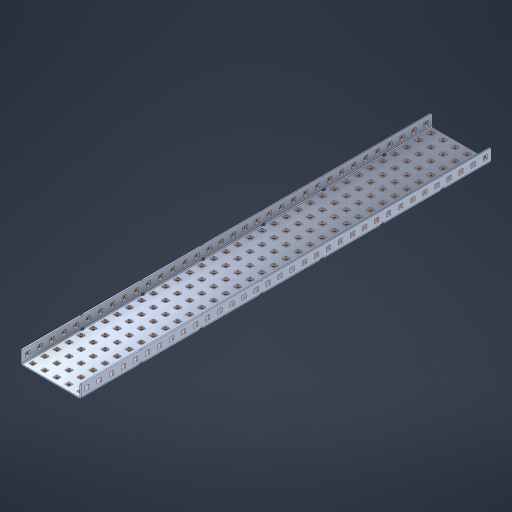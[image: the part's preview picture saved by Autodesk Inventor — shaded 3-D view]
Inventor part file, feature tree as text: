
AUTODESK INVENTOR PART (.ipt)
format: ipt  version: 2023 (Build 270158000, 158)  size: 2,476,032 bytes
history: native  units: in
note: dims shown in document units (in); Inventor stores cm internally (conversion verified against a paired STEP export)
features: other x243, extrude x237, sheet_metal_op x10, sketch x8, mirror x1, pattern_linear x1, chamfer x1
ambient origin geometry x8: Origin, YZ Plane, XZ Plane, XY Plane, X Axis, Y Axis, Z Axis, Center Point
bodies: Solid1 (feature_tree), Body (feature_tree)
feature tree (501):
  other  "Flange Pattern Plane"
  sheet_metal_op  "Flange Pattern"
  sheet_metal_op  "Body Pattern"
  other  "Arc Length"
  mirror  "Notch Mirror"
  pattern_linear  "Notch Pattern"  Spacing1=0.1875in  [1 undecoded]
  chamfer  "End Chamfer"
  extrude  "Half Cut"  Depth=0.0469in
  sketch  "Sketch1"  dims[d0=2.5in]
  other  "Plate1"
  sketch  "Sketch2"  dims[d1=17.0in]
  other  "Plate2"
  sheet_metal_op  "Bend1"
  sheet_metal_op  "Corner1"
  sketch  "Sketch3"  dims[d2=0.0469in]
  other  "Flange Pattern Sketch"
  sketch  "Sketch7"  dims[d3=0.0469in]
  other  "Srf1"
  other  "Srf2"
  sketch  "Sketch8"  dims[d4=0.0234in]
  sketch  "Sketch9"  dims[d5=0.0938in]
  other  "Srf91"
  sheet_metal_op  "Body Pattern Sketch"
  other  "Srf92"
  sketch  "Sketch13"  dims[d6=0.0469in]
  sketch  "Sketch14"  dims[d7=0.5in d8=90.0deg d9=0.0312in d10=0.1875in d11=0.0469in d12=0.0469in d16=0.182in d17=0.02in d18=0.0469in d19=0.0in d20=0.25in d21=0.25in d46=0.172in d47=1.0in d48=0.0in d49=0.182in d50=0.02in d51=0.25in d52=0.25in d53=0.0469in d54=0.0in d55=0.172in d56=1.0in d57=0.0in d60=13.3858in d62=0.5in d63=1.9685in d65=0.5in d85=0.1227in d86=0.1659in d88=0.04in d89=0.0469in d90=0.0in d91=0.04in d92=0.0491in d95=2.5in d96=0.04in d97=0.25in d98=45.0deg d101=0.0in d102=2.497in d131=2.5in d132=13.3858in d134=0.5in d139=0.5in]
  other  "Srf856"
  other  "Srf1310"
  other  "Srf1311"
  other  "Srf1312"
  other  "Srf1376"
  other  "Srf1377"
  other  "Srf1728"
  other  "Srf1755"
  other  "Srf1878"
  other  "Srf1879"
  other  "Srf1880"
  other  "Srf1881"
  other  "Srf1882"
  other  "Srf1883"
  other  "Srf1884"
  other  "Srf1885"
  other  "Srf1886"
  other  "Srf1887"
  other  "Srf1888"
  other  "Srf1889"
  other  "Srf1890"
  other  "Srf1891"
  other  "Srf1892"
  other  "Srf1893"
  other  "Srf1894"
  other  "Srf1895"
  other  "Srf1896"
  other  "Srf1897"
  other  "Srf1898"
  other  "Srf1899"
  other  "Srf1900"
  other  "Srf1901"
  other  "Srf1902"
  other  "Srf1903"
  other  "Srf1904"
  other  "Srf1905"
  other  "Srf1906"
  other  "Srf1942"
  other  "Srf1943"
  other  "Srf1944"
  other  "Srf1945"
  other  "Srf1946"
  other  "Srf1947"
  other  "Srf1948"
  other  "Srf1949"
  other  "Srf1950"
  other  "Srf1951"
  other  "Srf1952"
  other  "Srf1953"
  other  "Srf1954"
  other  "Srf1955"
  other  "Srf1956"
  other  "Srf1957"
  other  "Srf1958"
  other  "Srf1959"
  other  "Srf1960"
  other  "Srf1961"
  other  "Srf1962"
  other  "Srf1963"
  other  "Srf1964"
  other  "Srf1965"
  other  "Srf1966"
  other  "Srf1967"
  other  "Srf1968"
  other  "Srf1969"
  other  "Srf1970"
  other  "Srf2111"
  other  "Srf2112"
  other  "Srf2113"
  other  "Srf2114"
  other  "Srf2115"
  other  "Srf2116"
  other  "Srf2117"
  other  "Srf2118"
  other  "Srf2119"
  other  "Srf2120"
  other  "Srf2121"
  other  "Srf2122"
  other  "Srf2123"
  other  "Srf2124"
  other  "Srf2125"
  other  "Srf2126"
  other  "Srf2127"
  other  "Srf2128"
  other  "Srf2129"
  other  "Srf2130"
  other  "Srf2131"
  other  "Srf2132"
  other  "Srf2133"
  other  "Srf2134"
  other  "Srf2135"
  other  "Srf2136"
  other  "Srf2137"
  other  "Srf2138"
  other  "Srf2139"
  other  "Srf2140"
  other  "Srf2141"
  other  "Srf2142"
  other  "Srf2143"
  other  "Srf2146"
  other  "Srf2147"
  other  "Srf2148"
  other  "Srf2149"
  other  "Srf2150"
  other  "Srf2151"
  other  "Srf2152"
  other  "Srf2153"
  other  "Srf2154"
  other  "Srf2155"
  other  "Srf2156"
  other  "Srf2157"
  other  "Srf2158"
  other  "Srf2159"
  other  "Srf2160"
  other  "Srf2161"
  other  "Srf2162"
  other  "Srf2163"
  other  "Srf2164"
  other  "Srf2165"
  other  "Srf2166"
  other  "Srf2167"
  other  "Srf2168"
  other  "Srf2169"
  other  "Srf2170"
  other  "Srf2171"
  other  "Srf2172"
  other  "Srf2173"
  other  "Srf2174"
  other  "Srf2175"
  other  "Srf2176"
  other  "Srf2177"
  other  "Srf2178"
  other  "Srf2179"
  other  "Srf2180"
  other  "Srf2181"
  other  "Srf2182"
  other  "Srf2183"
  other  "Srf2184"
  other  "Srf2185"
  other  "Srf2186"
  other  "Srf2187"
  other  "Srf2188"
  other  "Srf2189"
  other  "Srf2190"
  other  "Srf2191"
  other  "Srf2192"
  other  "Srf2193"
  other  "Srf2194"
  other  "Srf2195"
  other  "Srf2196"
  other  "Srf2197"
  other  "Srf2198"
  other  "Srf2199"
  other  "Srf2200"
  other  "Srf2201"
  other  "Srf2202"
  other  "Srf2203"
  other  "Srf2204"
  other  "Srf2205"
  other  "Srf2206"
  other  "Srf2207"
  other  "Srf2208"
  other  "Srf2209"
  other  "Srf2210"
  other  "Srf2211"
  other  "Srf2212"
  other  "Srf2213"
  other  "Srf2214"
  other  "Srf2215"
  other  "Srf2216"
  other  "Srf2217"
  other  "Srf2218"
  other  "Srf2219"
  other  "Srf2220"
  other  "Srf2221"
  other  "Srf2222"
  other  "Srf2223"
  other  "Srf2224"
  other  "Srf2225"
  other  "Srf2226"
  other  "Srf2227"
  other  "Srf2228"
  other  "Srf2229"
  other  "Srf2230"
  other  "Srf2231"
  other  "Srf2232"
  other  "Srf2233"
  other  "Srf2234"
  other  "Srf2235"
  other  "Srf2236"
  other  "Srf2237"
  other  "Srf2238"
  other  "Srf2239"
  other  "Srf2240"
  other  "Srf2241"
  other  "Srf2242"
  other  "Srf2243"
  other  "Srf2244"
  other  "Srf2245"
  other  "Srf2246"
  other  "Srf2247"
  other  "Srf2248"
  other  "Srf2249"
  other  "Srf2250"
  other  "Srf2251"
  other  "Srf2252"
  other  "Srf2253"
  other  "Srf2254"
  other  "Srf2255"
  other  "Srf2256"
  other  "Srf2257"
  other  "Srf2258"
  other  "Srf2259"
  other  "Srf2260"
  other  "Srf2261"
  other  "Srf2262"
  other  "Srf2263"
  other  "Srf2264"
  other  "Srf2265"
  other  "Srf2266"
  other  "Srf2267"
  other  "Srf2268"
  other  "Srf2269"
  other  "Srf2270"
  other  "Srf2271"
  other  "Srf2272"
  other  "Srf2273"
  other  "Srf2274"
  other  "Srf2275"
  other  "Srf2276"
  other  "Srf2277"
  other  "Srf2278"
  other  "Srf2279"
  other  "Srf2280"
  sheet_metal_op  "Flange Stamp"
  sheet_metal_op  "Flange Circle"
  sheet_metal_op  "Body Stamp"
  sheet_metal_op  "Body Circle"
  sheet_metal_op  "Notch"
  extrude  "ExtrusionSrf2"  Depth=0.0469in
  extrude  "ExtrusionSrf92"  Depth=2.5in
  extrude  "ExtrusionSrf856"  Depth=0.02in
  extrude  "ExtrusionSrf1310"  Depth=0.0469in
  extrude  "ExtrusionSrf1311"  TaperAngle=0.0deg  [1 undecoded]
  extrude  "ExtrusionSrf1312"  Depth=0.25in
  extrude  "ExtrusionSrf1376"  Depth=0.25in
  extrude  "ExtrusionSrf1377"  Depth=2.5in
  extrude  "ExtrusionSrf1728"  Depth=2.5in TaperAngle=0.0deg
  extrude  "ExtrusionSrf1755"  Depth=2.5in
  extrude  "ExtrusionSrf1878"  Depth=0.02in
  extrude  "ExtrusionSrf1879"  Depth=0.25in
  extrude  "ExtrusionSrf1880"  Depth=0.25in
  extrude  "ExtrusionSrf1881"  Depth=0.0469in
  extrude  "ExtrusionSrf1882"  TaperAngle=0.0deg  [1 undecoded]
  extrude  "ExtrusionSrf1883"  Depth=2.5in
  extrude  "ExtrusionSrf1884"  Depth=2.5in TaperAngle=0.0deg
  extrude  "ExtrusionSrf1885"  Depth=2.5in
  extrude  "ExtrusionSrf1886"  Depth=2.5in
  extrude  "ExtrusionSrf1887"  Depth=2.5in
  extrude  "ExtrusionSrf1888"  Depth=2.5in
  extrude  "ExtrusionSrf1889"  Depth=2.5in
  extrude  "ExtrusionSrf1890"  Depth=0.0469in
  extrude  "ExtrusionSrf1891"  TaperAngle=0.0deg  [1 undecoded]
  extrude  "ExtrusionSrf1892"  Depth=2.5in
  extrude  "ExtrusionSrf1893"  Depth=2.5in
  extrude  "ExtrusionSrf1894"  Depth=2.5in
  extrude  "ExtrusionSrf1895"  Depth=0.25in TaperAngle=45.0deg
  extrude  "ExtrusionSrf1896"  TaperAngle=0.0deg  [1 undecoded]
  extrude  "ExtrusionSrf1897"  Depth=2.5in
  extrude  "ExtrusionSrf1898"  Depth=2.5in
  extrude  "ExtrusionSrf1899"  Depth=2.5in
  extrude  "ExtrusionSrf1900"  Depth=2.5in
  extrude  "ExtrusionSrf1901"  Depth=2.5in
  extrude  "ExtrusionSrf1902"  [1 undecoded]
  extrude  "ExtrusionSrf1903"  [1 undecoded]
  extrude  "ExtrusionSrf1904"  [1 undecoded]
  extrude  "ExtrusionSrf1905"  [1 undecoded]
  extrude  "ExtrusionSrf1906"  [1 undecoded]
  extrude  "ExtrusionSrf1942"  [1 undecoded]
  extrude  "ExtrusionSrf1943"  [1 undecoded]
  extrude  "ExtrusionSrf1944"  [1 undecoded]
  extrude  "ExtrusionSrf1945"  [1 undecoded]
  extrude  "ExtrusionSrf1946"  [1 undecoded]
  extrude  "ExtrusionSrf1947"  [1 undecoded]
  extrude  "ExtrusionSrf1948"  [1 undecoded]
  extrude  "ExtrusionSrf1949"  [1 undecoded]
  extrude  "ExtrusionSrf1950"  [1 undecoded]
  extrude  "ExtrusionSrf1951"  [1 undecoded]
  extrude  "ExtrusionSrf1952"  [1 undecoded]
  extrude  "ExtrusionSrf1953"  [1 undecoded]
  extrude  "ExtrusionSrf1954"  [1 undecoded]
  extrude  "ExtrusionSrf1955"  [1 undecoded]
  extrude  "ExtrusionSrf1956"  [1 undecoded]
  extrude  "ExtrusionSrf1957"  [1 undecoded]
  extrude  "ExtrusionSrf1958"  [1 undecoded]
  extrude  "ExtrusionSrf1959"  [1 undecoded]
  extrude  "ExtrusionSrf1960"  [1 undecoded]
  extrude  "ExtrusionSrf1961"  [1 undecoded]
  extrude  "ExtrusionSrf1962"  [1 undecoded]
  extrude  "ExtrusionSrf1963"  [1 undecoded]
  extrude  "ExtrusionSrf1964"  [1 undecoded]
  extrude  "ExtrusionSrf1965"  [1 undecoded]
  extrude  "ExtrusionSrf1966"  [1 undecoded]
  extrude  "ExtrusionSrf1967"  [1 undecoded]
  extrude  "ExtrusionSrf1968"  [1 undecoded]
  extrude  "ExtrusionSrf1969"  [1 undecoded]
  extrude  "ExtrusionSrf1970"  [1 undecoded]
  extrude  "ExtrusionSrf2111"  [1 undecoded]
  extrude  "ExtrusionSrf2112"  [1 undecoded]
  extrude  "ExtrusionSrf2113"  [1 undecoded]
  extrude  "ExtrusionSrf2114"  [1 undecoded]
  extrude  "ExtrusionSrf2115"  [1 undecoded]
  extrude  "ExtrusionSrf2116"  [1 undecoded]
  extrude  "ExtrusionSrf2117"  [1 undecoded]
  extrude  "ExtrusionSrf2118"  [1 undecoded]
  extrude  "ExtrusionSrf2119"  [1 undecoded]
  extrude  "ExtrusionSrf2120"  [1 undecoded]
  extrude  "ExtrusionSrf2121"  [1 undecoded]
  extrude  "ExtrusionSrf2122"  [1 undecoded]
  extrude  "ExtrusionSrf2123"  [1 undecoded]
  extrude  "ExtrusionSrf2124"  [1 undecoded]
  extrude  "ExtrusionSrf2125"  [1 undecoded]
  extrude  "ExtrusionSrf2126"  [1 undecoded]
  extrude  "ExtrusionSrf2127"  [1 undecoded]
  extrude  "ExtrusionSrf2128"  [1 undecoded]
  extrude  "ExtrusionSrf2129"  [1 undecoded]
  extrude  "ExtrusionSrf2130"  [1 undecoded]
  extrude  "ExtrusionSrf2131"  [1 undecoded]
  extrude  "ExtrusionSrf2132"  [1 undecoded]
  extrude  "ExtrusionSrf2133"  [1 undecoded]
  extrude  "ExtrusionSrf2134"  [1 undecoded]
  extrude  "ExtrusionSrf2135"  [1 undecoded]
  extrude  "ExtrusionSrf2136"  [1 undecoded]
  extrude  "ExtrusionSrf2137"  [1 undecoded]
  extrude  "ExtrusionSrf2138"  [1 undecoded]
  extrude  "ExtrusionSrf2139"  [1 undecoded]
  extrude  "ExtrusionSrf2140"  [1 undecoded]
  extrude  "ExtrusionSrf2141"  [1 undecoded]
  extrude  "ExtrusionSrf2142"  [1 undecoded]
  extrude  "ExtrusionSrf2143"  [1 undecoded]
  extrude  "ExtrusionSrf2146"  [1 undecoded]
  extrude  "ExtrusionSrf2147"  [1 undecoded]
  extrude  "ExtrusionSrf2148"  [1 undecoded]
  extrude  "ExtrusionSrf2149"  [1 undecoded]
  extrude  "ExtrusionSrf2150"  [1 undecoded]
  extrude  "ExtrusionSrf2151"  [1 undecoded]
  extrude  "ExtrusionSrf2152"  [1 undecoded]
  extrude  "ExtrusionSrf2153"  [1 undecoded]
  extrude  "ExtrusionSrf2154"  [1 undecoded]
  extrude  "ExtrusionSrf2155"  [1 undecoded]
  extrude  "ExtrusionSrf2156"  [1 undecoded]
  extrude  "ExtrusionSrf2157"  [1 undecoded]
  extrude  "ExtrusionSrf2158"  [1 undecoded]
  extrude  "ExtrusionSrf2159"  [1 undecoded]
  extrude  "ExtrusionSrf2160"  [1 undecoded]
  extrude  "ExtrusionSrf2161"  [1 undecoded]
  extrude  "ExtrusionSrf2162"  [1 undecoded]
  extrude  "ExtrusionSrf2163"  [1 undecoded]
  extrude  "ExtrusionSrf2164"  [1 undecoded]
  extrude  "ExtrusionSrf2165"  [1 undecoded]
  extrude  "ExtrusionSrf2166"  [1 undecoded]
  extrude  "ExtrusionSrf2167"  [1 undecoded]
  extrude  "ExtrusionSrf2168"  [1 undecoded]
  extrude  "ExtrusionSrf2169"  [1 undecoded]
  extrude  "ExtrusionSrf2170"  [1 undecoded]
  extrude  "ExtrusionSrf2171"  [1 undecoded]
  extrude  "ExtrusionSrf2172"  [1 undecoded]
  extrude  "ExtrusionSrf2173"  [1 undecoded]
  extrude  "ExtrusionSrf2174"  [1 undecoded]
  extrude  "ExtrusionSrf2175"  [1 undecoded]
  extrude  "ExtrusionSrf2176"  [1 undecoded]
  extrude  "ExtrusionSrf2177"  [1 undecoded]
  extrude  "ExtrusionSrf2178"  [1 undecoded]
  extrude  "ExtrusionSrf2179"  [1 undecoded]
  extrude  "ExtrusionSrf2180"  [1 undecoded]
  extrude  "ExtrusionSrf2181"  [1 undecoded]
  extrude  "ExtrusionSrf2182"  [1 undecoded]
  extrude  "ExtrusionSrf2183"  [1 undecoded]
  extrude  "ExtrusionSrf2184"  [1 undecoded]
  extrude  "ExtrusionSrf2185"  [1 undecoded]
  extrude  "ExtrusionSrf2186"  [1 undecoded]
  extrude  "ExtrusionSrf2187"  [1 undecoded]
  extrude  "ExtrusionSrf2188"  [1 undecoded]
  extrude  "ExtrusionSrf2189"  [1 undecoded]
  extrude  "ExtrusionSrf2190"  [1 undecoded]
  extrude  "ExtrusionSrf2191"  [1 undecoded]
  extrude  "ExtrusionSrf2192"  [1 undecoded]
  extrude  "ExtrusionSrf2193"  [1 undecoded]
  extrude  "ExtrusionSrf2194"  [1 undecoded]
  extrude  "ExtrusionSrf2195"  [1 undecoded]
  extrude  "ExtrusionSrf2196"  [1 undecoded]
  extrude  "ExtrusionSrf2197"  [1 undecoded]
  extrude  "ExtrusionSrf2198"  [1 undecoded]
  extrude  "ExtrusionSrf2199"  [1 undecoded]
  extrude  "ExtrusionSrf2200"  [1 undecoded]
  extrude  "ExtrusionSrf2201"  [1 undecoded]
  extrude  "ExtrusionSrf2202"  [1 undecoded]
  extrude  "ExtrusionSrf2203"  [1 undecoded]
  extrude  "ExtrusionSrf2204"  [1 undecoded]
  extrude  "ExtrusionSrf2205"  [1 undecoded]
  extrude  "ExtrusionSrf2206"  [1 undecoded]
  extrude  "ExtrusionSrf2207"  [1 undecoded]
  extrude  "ExtrusionSrf2208"  [1 undecoded]
  extrude  "ExtrusionSrf2209"  [1 undecoded]
  extrude  "ExtrusionSrf2210"  [1 undecoded]
  extrude  "ExtrusionSrf2211"  [1 undecoded]
  extrude  "ExtrusionSrf2212"  [1 undecoded]
  extrude  "ExtrusionSrf2213"  [1 undecoded]
  extrude  "ExtrusionSrf2214"  [1 undecoded]
  extrude  "ExtrusionSrf2215"  [1 undecoded]
  extrude  "ExtrusionSrf2216"  [1 undecoded]
  extrude  "ExtrusionSrf2217"  [1 undecoded]
  extrude  "ExtrusionSrf2218"  [1 undecoded]
  extrude  "ExtrusionSrf2219"  [1 undecoded]
  extrude  "ExtrusionSrf2220"  [1 undecoded]
  extrude  "ExtrusionSrf2221"  [1 undecoded]
  extrude  "ExtrusionSrf2222"  [1 undecoded]
  extrude  "ExtrusionSrf2223"  [1 undecoded]
  extrude  "ExtrusionSrf2224"  [1 undecoded]
  extrude  "ExtrusionSrf2225"  [1 undecoded]
  extrude  "ExtrusionSrf2226"  [1 undecoded]
  extrude  "ExtrusionSrf2227"  [1 undecoded]
  extrude  "ExtrusionSrf2228"  [1 undecoded]
  extrude  "ExtrusionSrf2229"  [1 undecoded]
  extrude  "ExtrusionSrf2230"  [1 undecoded]
  extrude  "ExtrusionSrf2231"  [1 undecoded]
  extrude  "ExtrusionSrf2232"  [1 undecoded]
  extrude  "ExtrusionSrf2233"  [1 undecoded]
  extrude  "ExtrusionSrf2234"  [1 undecoded]
  extrude  "ExtrusionSrf2235"  [1 undecoded]
  extrude  "ExtrusionSrf2236"  [1 undecoded]
  extrude  "ExtrusionSrf2237"  [1 undecoded]
  extrude  "ExtrusionSrf2238"  [1 undecoded]
  extrude  "ExtrusionSrf2239"  [1 undecoded]
  extrude  "ExtrusionSrf2240"  [1 undecoded]
  extrude  "ExtrusionSrf2241"  [1 undecoded]
  extrude  "ExtrusionSrf2242"  [1 undecoded]
  extrude  "ExtrusionSrf2243"  [1 undecoded]
  extrude  "ExtrusionSrf2244"  [1 undecoded]
  extrude  "ExtrusionSrf2245"  [1 undecoded]
  extrude  "ExtrusionSrf2246"  [1 undecoded]
  extrude  "ExtrusionSrf2247"  [1 undecoded]
  extrude  "ExtrusionSrf2248"  [1 undecoded]
  extrude  "ExtrusionSrf2249"  [1 undecoded]
  extrude  "ExtrusionSrf2250"  [1 undecoded]
  extrude  "ExtrusionSrf2251"  [1 undecoded]
  extrude  "ExtrusionSrf2252"  [1 undecoded]
  extrude  "ExtrusionSrf2253"  [1 undecoded]
  extrude  "ExtrusionSrf2254"  [1 undecoded]
  extrude  "ExtrusionSrf2255"  [1 undecoded]
  extrude  "ExtrusionSrf2256"  [1 undecoded]
  extrude  "ExtrusionSrf2257"  [1 undecoded]
  extrude  "ExtrusionSrf2258"  [1 undecoded]
  extrude  "ExtrusionSrf2259"  [1 undecoded]
  extrude  "ExtrusionSrf2260"  [1 undecoded]
  extrude  "ExtrusionSrf2261"  [1 undecoded]
  extrude  "ExtrusionSrf2262"  [1 undecoded]
  extrude  "ExtrusionSrf2263"  [1 undecoded]
  extrude  "ExtrusionSrf2264"  [1 undecoded]
  extrude  "ExtrusionSrf2265"  [1 undecoded]
  extrude  "ExtrusionSrf2266"  [1 undecoded]
  extrude  "ExtrusionSrf2267"  [1 undecoded]
  extrude  "ExtrusionSrf2268"  [1 undecoded]
  extrude  "ExtrusionSrf2269"  [1 undecoded]
  extrude  "ExtrusionSrf2270"  [1 undecoded]
  extrude  "ExtrusionSrf2271"  [1 undecoded]
  extrude  "ExtrusionSrf2272"  [1 undecoded]
  extrude  "ExtrusionSrf2273"  [1 undecoded]
  extrude  "ExtrusionSrf2274"  [1 undecoded]
  extrude  "ExtrusionSrf2275"  [1 undecoded]
  extrude  "ExtrusionSrf2276"  [1 undecoded]
  extrude  "ExtrusionSrf2277"  [1 undecoded]
  extrude  "ExtrusionSrf2278"  [1 undecoded]
  extrude  "ExtrusionSrf2279"  [1 undecoded]
  extrude  "ExtrusionSrf2280"  [1 undecoded]
note: 207 required parameter values undecoded (feature->parameter linkage not recoverable at this tier; creation-order binding heuristic only, values carry confidence <= 0.55)
